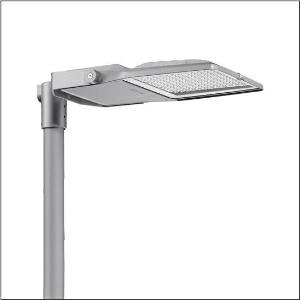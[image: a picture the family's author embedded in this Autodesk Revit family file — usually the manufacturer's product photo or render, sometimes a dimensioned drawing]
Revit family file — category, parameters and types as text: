
# Revit family: floodlight_fl_21_iq_midi___pl64_5xa7782f4e3a_0b41
name_source: partatom
category: Lighting Fixtures
units: mm (PartAtom-declared; Revit-internal decimal feet)

## family parameters
Cut with Voids When Loaded = No
Host = Face
Light Source = No
Part Type = Normal
Room Calculation Point = No
Round Connector Dimension = Use Diameter
Shared = No

## types (1)
- --- (1 x LED, 36050 lm, 270.2 W, 4000K)
    Apparent Load = 270 VA
    CIE Flux Codes = 28 80 98 100 100
    Color Rendering = 70
    Color Temperature = 4000K
    Default Elevation = 1800 mm
    Description = Floodlight FL 21 iQ midi, floodlight, primary light control with lens, of PMMA, primary optical cover: protective disc, of toughened safety glass, transparent, light distribution: PL64, light emission: direct distribution, installation type: surface-mounted, LED, High Power LED, rated luminous flux: 36.050lm, luminous efficacy: 133lm/W, light colour: 740, colour temperature: 4000K, control gear: ECG iQ, control: optimised constant luminous flux control (CLO 2.0), Desk-Remote (wireless, voltage-free reading and setting of iQ features in the workshop via application-optimized NFC function/RFID function), Smart-Wire, Night-Set, Temp-Guard, Auto-Match, Street-Remote, with terminal, 6-pole, mains connection: 220..240V, AC, 50/60Hz, start of lifetime: 270W, end of service life: 287W, reduction: 118W, luminaire housing, of diecast aluminium, powder-coated, Siteco® metallic grey (DB 702S), corrosivity category C5 mid according to DIN EN ISO 12944, sealing non-destructively replaceable, please order mast flange separately, mast bracket, of steel, galvanised, powder-coated, Siteco® metallic grey (DB 702S), protection rating (complete): IP66, insulation class (complete): insulation class II (safety insulation), certification: CE, protection symbol: D, impact resistance: IK08, permissible operating ambient temperature: -40..+40°C, permissible operating ambient temperature for outdoor applications: -40..+50°C, standard: DIN EN 12944, LABS conformity tested according to VDMA 24364:2018-05, packaging unit: 1 piece

Light Distribution: PL64
    Height = 76 mm
    Lamp = 1 x LED
    Lamp Light Flux = 36050 lm
    Lamp Power = 270.2 W
    Lamp count = 1
    Length = 657 mm
    Luminous efficacy = 133 lm/W
    Manufacturer = Siteco
    ModVariant = No
    Model = 5XA7782F4E3A
    Number of Poles = 1
    OnlyDefault = Yes
    Power Factor = 1
    Product Name = Floodlight FL 21 iQ midi | PL64
    Product group = floodlight | pylon annexe
    ProductGroupID = 6200
    Protection Class = Protection class II
    Protection Degree = IP 66
    RLX_Detail_Level = 1
    RLX_Emergency_Light_Flux = 0 lm
    RLX_Emergency_Type = 0
    RLX_Emergency_Type_DB = No
    RlxData = <blob elided: 153649 chars, md5=d24525cb>
    Socket = socket
    Standby Power = 0 W
    System Light Flux = 36050 lm
    System Power = 270 W
    Type Comments = factory setting: luminous flux: 100 % | dim-lin: 254 | 620 mA
    Type Image = l_1007123.jpg
    URL = http://relux.com
    VarID = @adj_036691
    Voltage = 0 V
    Weight = 0.00 kg
    Width = 442 mm

## geometry (parser evidence)
native form markers: Blend x4, Sweep x14
no freeform markers — native parametric forms only
